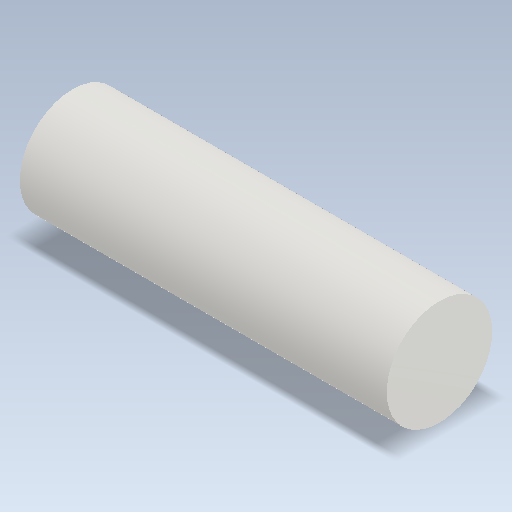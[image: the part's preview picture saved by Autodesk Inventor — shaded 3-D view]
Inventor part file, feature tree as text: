
AUTODESK INVENTOR PART (.ipt)
format: ipt  version: 2021 (Build 250183000, 183)  size: 119,296 bytes
history: native  units: mm
features: other x1, extrude x1, sketch x1
ambient origin geometry x8: Origin, YZ Plane, XZ Plane, XY Plane, X Axis, Y Axis, Z Axis, Center Point
bodies: Body1 (feature_tree)
feature tree (3):
  other  "Sólido1"
  extrude  "Extrusión1"  TaperAngle=0.0deg  [1 undecoded]
  sketch  "Boceto1"  dims[d0=8.0mm d1=0.0mm d2=2.3mm]
note: 1 required parameter value undecoded (feature->parameter linkage not recoverable at this tier; creation-order binding heuristic only, values carry confidence <= 0.55)
